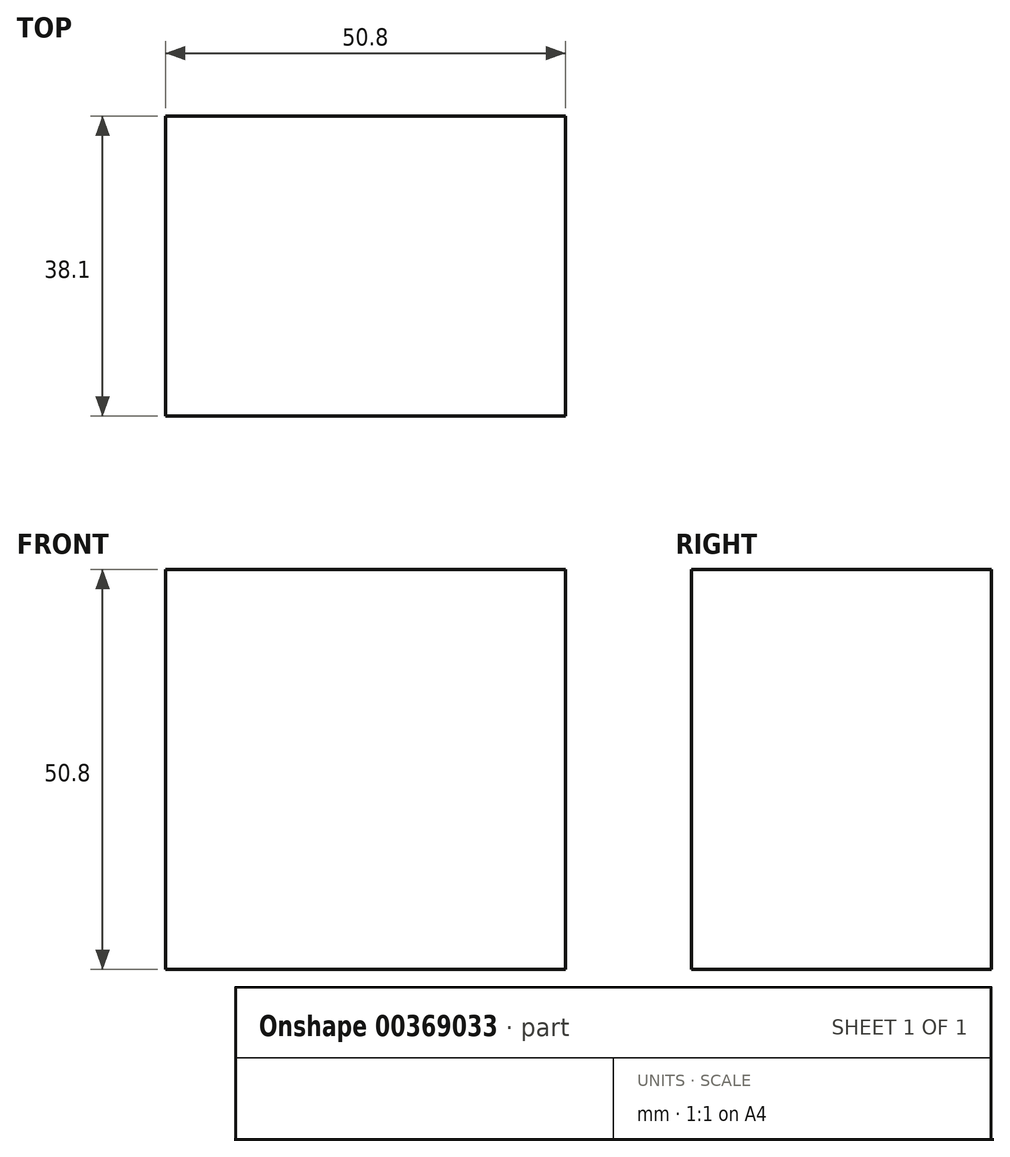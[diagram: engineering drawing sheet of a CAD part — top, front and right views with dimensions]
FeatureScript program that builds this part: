
annotation { "Feature Type Name" : "Feature", "Feature Type Description" : "" }
export const myFeature = defineFeature(function(context is Context, id is Id, definition is map)
    precondition{}
    {
        {
            var Q0;
            Q0=qCreatedBy(makeId("Front.planeOp"),FACE);
            var sketch = newSketch(context, id + "F0", { "sketchPlane" : qUnion([Q0])});
            skLineSegment(sketch, "E0", {"start": v(0, 0) * mm, "end": v(50.8, 0) * mm});
            skLineSegment(sketch, "E1", {"start": v(50.8, 0) * mm, "end": v(50.8, 50.8) * mm});
            skLineSegment(sketch, "E2", {"start": v(50.8, 50.8) * mm, "end": v(0, 50.8) * mm});
            skLineSegment(sketch, "E3", {"start": v(0, 50.8) * mm, "end": v(0, 0) * mm});
            skSolve(sketch);
        }
        {
            var Q0;
            Q0=makeQuery(id+"F0.imprint","IMPRINT",FACE,{"disambiguationData":[TD([[makeQuery(id+"F0.imprint","IMPRINT",EDGE,{"derivedFrom":sQuery(id+"F0.wireOp",EDGE,"E0")}),1.0]])]});
            extrude(context, id + "F1", {"entities" : qUnion([Q0]), "depth" : 38.1 * mm});
        }
    });
